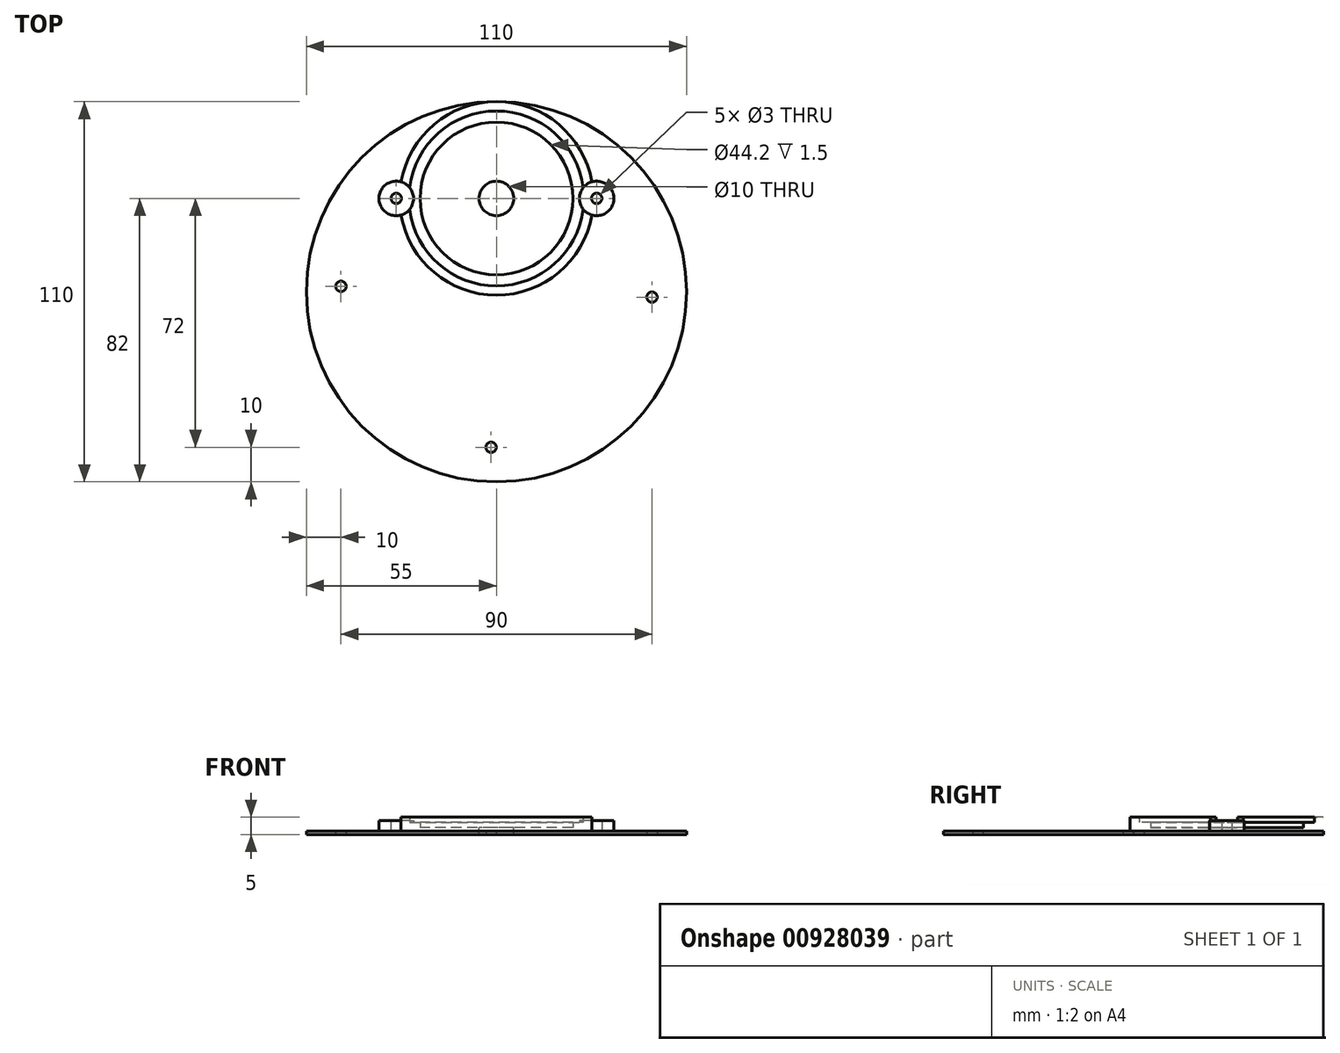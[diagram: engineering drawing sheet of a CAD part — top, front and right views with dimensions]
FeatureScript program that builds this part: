
annotation { "Feature Type Name" : "Feature", "Feature Type Description" : "" }
export const myFeature = defineFeature(function(context is Context, id is Id, definition is map)
    precondition{}
    {
        {
            var Q0;
            Q0=qCreatedBy(makeId("Top.planeOp"),FACE);
            var sketch = newSketch(context, id + "F0", { "sketchPlane" : qUnion([Q0])});
            skCircle(sketch, "E0", {"center": v(0, 0) * mm, "radius": 28 * mm});
            skCircle(sketch, "E1", {"center": v(29, 0) * mm, "radius": 5 * mm});
            skCircle(sketch, "E2", {"center": v(29, 0) * mm, "radius": 1.5 * mm});
            skCircle(sketch, "E3.1.0", {"center": v(-29, 0) * mm, "radius": 5 * mm});
            skCircle(sketch, "E3.1.1", {"center": v(-29, 0) * mm, "radius": 1.5 * mm});
            skCircle(sketch, "E4", {"center": v(0, -27) * mm, "radius": 55 * mm});
            skLineSegment(sketch, "E5", {"start": v(-81.1, -27) * mm, "end": v(83.2, -29.03) * mm, "construction": true});
            skCircle(sketch, "E6", {"center": v(45, -28.56) * mm, "radius": 1.5 * mm});
            skCircle(sketch, "E7.1.0", {"center": v(1.56, 18) * mm, "radius": 1.5 * mm});
            skCircle(sketch, "E7.2.0", {"center": v(-45, -25.44) * mm, "radius": 1.5 * mm});
            skCircle(sketch, "E7.3.0", {"center": v(-1.56, -72) * mm, "radius": 1.5 * mm});
            skSolve(sketch);
        }
        {
            var Q0;
            Q0=makeQuery(id+"F0.imprint","IMPRINT",FACE,{"disambiguationData":[TD([[makeQuery(id+"F0.imprint","IMPRINT",EDGE,{"derivedFrom":sQuery(id+"F0.wireOp",EDGE,"E4")}),1.0]])]});
            var Q1;
            Q1=makeQuery(id+"F0.imprint","IMPRINT",FACE,{"disambiguationData":[TD([[makeQuery(id+"F0.imprint","IMPRINT",EDGE,{"derivedFrom":sQuery(id+"F0.wireOp",EDGE,"E7.1.0")}),-1.0]])]});
            var Q2;
            Q2=makeQuery(id+"F0.imprint","IMPRINT",FACE,{"disambiguationData":[TD([[makeQuery(id+"F0.imprint","IMPRINT",EDGE,{"derivedFrom":sQuery(id+"F0.wireOp",EDGE,"E7.1.0")}),1.0]])]});
            var Q3;
            {var subQ0=sQuery(id+"F0.wireOp",EDGE,"E3.1.0");var subQ1=sQuery(id+"F0.wireOp",EDGE,"E0");var subQ2=makeQuery(id+"F0.imprint","INTERSECT",VERTEX,{"disambiguationData":[OD(0.0)],"derivedFrom":[subQ1,subQ0]});Q3=makeQuery(id+"F0.imprint","IMPRINT",FACE,{"disambiguationData":[TD([[makeQuery(id+"F0.imprint","IMPRINT",EDGE,{"disambiguationData":[TD([[subQ2,-1.0]])],"derivedFrom":subQ1}),1.0]])]});}
            var Q4;
            {var subQ0=sQuery(id+"F0.wireOp",EDGE,"E1");var subQ1=sQuery(id+"F0.wireOp",EDGE,"E0");var subQ2=makeQuery(id+"F0.imprint","INTERSECT",VERTEX,{"disambiguationData":[OD(0.0)],"derivedFrom":[subQ1,subQ0]});Q4=makeQuery(id+"F0.imprint","IMPRINT",FACE,{"disambiguationData":[TD([[makeQuery(id+"F0.imprint","IMPRINT",EDGE,{"disambiguationData":[TD([[subQ2,1.0]])],"derivedFrom":subQ1}),1.0]])]});}
            extrude(context, id + "F1", {"entities" : qUnion([Q0, Q1, Q2, Q3, Q4]), "depth" : 1 * mm, "offsetDistance" : 25 * mm});
        }
        {
            var Q0;
            Q0=makeQuery(id+"F0.imprint","IMPRINT",FACE,{"disambiguationData":[TD([[makeQuery(id+"F0.imprint","IMPRINT",EDGE,{"derivedFrom":sQuery(id+"F0.wireOp",EDGE,"E3.1.1")}),-1.0]])]});
            var Q1;
            Q1=makeQuery(id+"F0.imprint","IMPRINT",FACE,{"disambiguationData":[TD([[makeQuery(id+"F0.imprint","IMPRINT",EDGE,{"derivedFrom":sQuery(id+"F0.wireOp",EDGE,"E2")}),-1.0]])]});
            extrude(context, id + "F2", {"entities" : qUnion([Q0, Q1]), "depth" : 4 * mm, "offsetDistance" : 25 * mm});
        }
        {
            var Q0;
            Q0=makeQuery(id+"F1.opExtrude","CAP_FACE",FACE,{"disambiguationData":[OSD([sQuery(id+"F0.wireOp",EDGE,"E0")])],"isStart":false});
            var sketch = newSketch(context, id + "F3", { "sketchPlane" : qUnion([Q0])});
            skCircle(sketch, "E8", {"center": v(0, 0) * mm, "radius": 22.1 * mm});
            skCircle(sketch, "E9", {"center": v(0, 0) * mm, "radius": 28 * mm});
            skSolve(sketch);
        }
        {
            var Q0;
            Q0=makeQuery(id+"F3.imprint","IMPRINT",FACE,{"disambiguationData":[TD([[makeQuery(id+"F3.imprint","IMPRINT",EDGE,{"derivedFrom":sQuery(id+"F3.wireOp",EDGE,"E8")}),1.0]])]});
            extrude(context, id + "F4", {"entities" : qUnion([Q0]), "operationType" : NewBodyOperationType.ADD, "depth" : 1 * mm, "offsetDistance" : 25 * mm});
        }
        {
            var Q0;
            Q0=makeQuery(id+"F3.imprint","IMPRINT",FACE,{"disambiguationData":[TD([[makeQuery(id+"F3.imprint","IMPRINT",EDGE,{"derivedFrom":sQuery(id+"F3.wireOp",EDGE,"E8")}),-1.0]])]});
            extrude(context, id + "F5", {"entities" : qUnion([Q0]), "operationType" : NewBodyOperationType.ADD, "depth" : 2.5 * mm, "offsetDistance" : 25 * mm});
        }
        {
            var Q0;
            Q0=makeQuery(id+"F5.opExtrude","CAP_FACE",FACE,{"disambiguationData":[OSD([sQuery(id+"F0.wireOp",EDGE,"E0"),sQuery(id+"F3.wireOp",EDGE,"E8")])],"isStart":false});
            var sketch = newSketch(context, id + "F6", { "sketchPlane" : qUnion([Q0])});
            skCircle(sketch, "E10", {"center": v(0, 0) * mm, "radius": 25.3 * mm});
            skSolve(sketch);
        }
        {
            var Q0;
            Q0=makeQuery(id+"F6.imprint","IMPRINT",FACE,{"disambiguationData":[TD([[makeQuery(id+"F6.imprint","IMPRINT",EDGE,{"derivedFrom":sQuery(id+"F6.wireOp",EDGE,"E10")}),-1.0]])]});
            extrude(context, id + "F7", {"entities" : qUnion([Q0]), "operationType" : NewBodyOperationType.ADD, "depth" : 1.5 * mm, "offsetDistance" : 25 * mm});
        }
        {
            var Q0;
            Q0=makeQuery(id+"F1.opExtrude","CAP_FACE",FACE,{"disambiguationData":[OSD([sQuery(id+"F0.wireOp",EDGE,"E0")])],"isStart":false});
            var sketch = newSketch(context, id + "F8", { "sketchPlane" : qUnion([Q0])});
            skCircle(sketch, "E11", {"center": v(0, 0) * mm, "radius": 5 * mm});
            skSolve(sketch);
        }
        {
            var Q0;
            Q0=makeQuery(id+"F8.imprint","IMPRINT",FACE,{"disambiguationData":[TD([[makeQuery(id+"F8.imprint","IMPRINT",EDGE,{"derivedFrom":sQuery(id+"F8.wireOp",EDGE,"E11")}),1.0]])]});
            extrude(context, id + "F9", {"entities" : qUnion([Q0]), "operationType" : NewBodyOperationType.REMOVE, "endBound" : BoundingType.SYMMETRIC, "oppositeDirection" : true, "depth" : 25 * mm, "offsetDistance" : 25 * mm});
        }
    });
